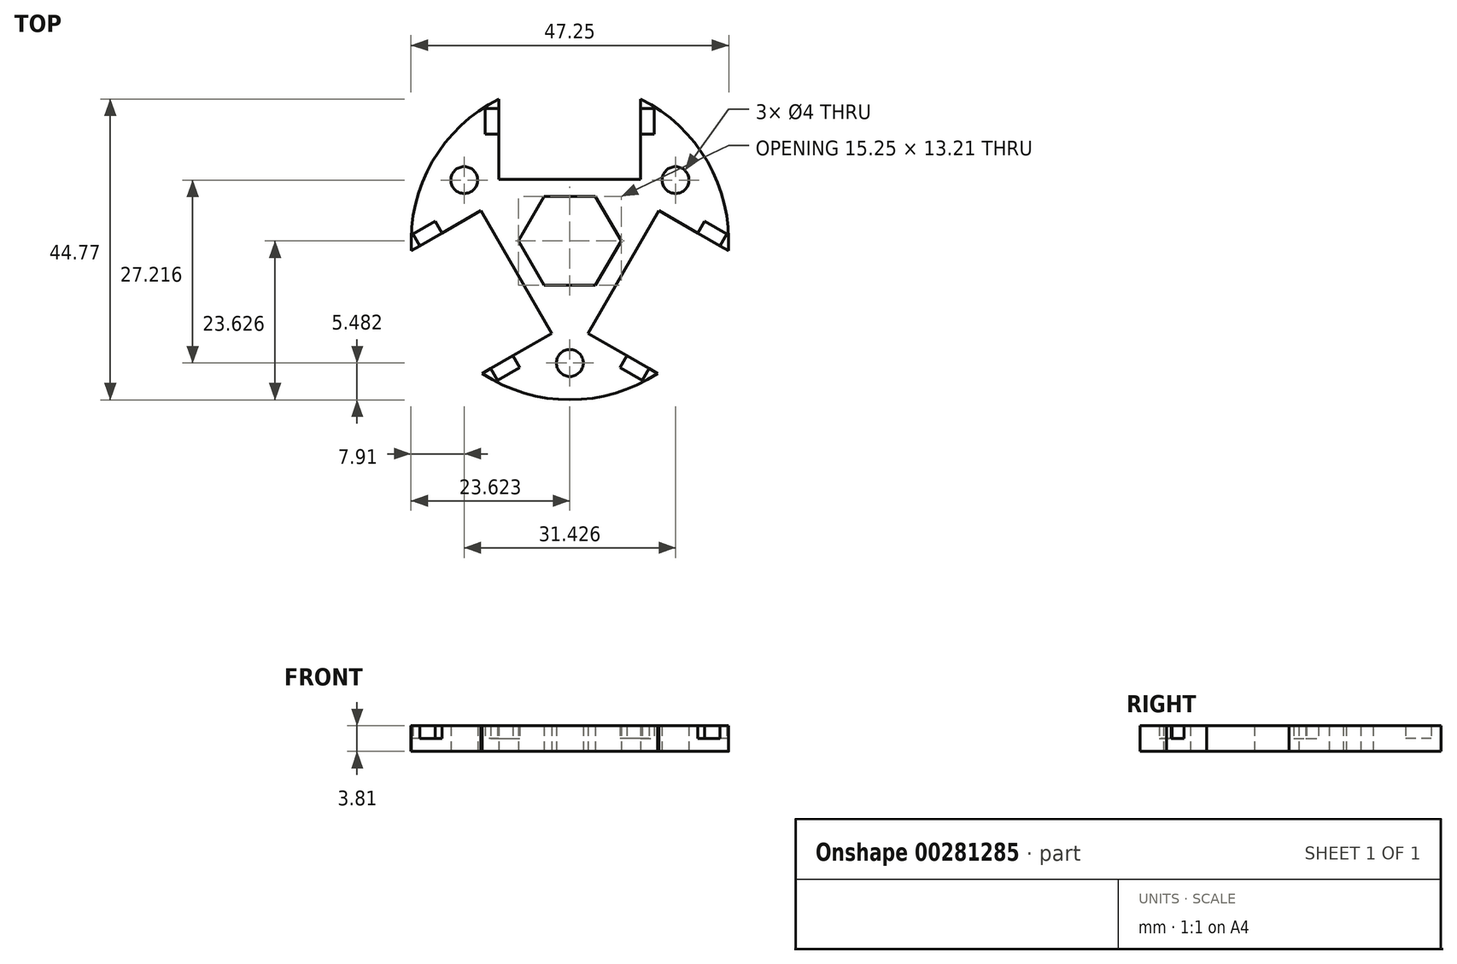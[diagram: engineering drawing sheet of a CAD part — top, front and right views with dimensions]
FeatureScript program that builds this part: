
annotation { "Feature Type Name" : "Feature", "Feature Type Description" : "" }
export const myFeature = defineFeature(function(context is Context, id is Id, definition is map)
    precondition{}
    {
        {
            var Q0;
            Q0=qCreatedBy(makeId("Top.planeOp"),FACE);
            var sketch = newSketch(context, id + "F0", { "sketchPlane" : qUnion([Q0])});
            skCircle(sketch, "E0.cCircle", {"center": v(-0.3, 28.84) * mm, "radius": 6.6 * mm, "construction": true});
            skLineSegment(sketch, "E0.0", {"start": v(-4.12, 35.44) * mm, "end": v(3.5, 35.44) * mm});
            skLineSegment(sketch, "E0.1", {"start": v(3.5, 35.44) * mm, "end": v(7.32, 28.84) * mm});
            skLineSegment(sketch, "E0.2", {"start": v(7.32, 28.84) * mm, "end": v(3.5, 22.23) * mm});
            skLineSegment(sketch, "E0.3", {"start": v(3.5, 22.23) * mm, "end": v(-4.12, 22.23) * mm});
            skLineSegment(sketch, "E0.4", {"start": v(-4.12, 22.23) * mm, "end": v(-7.93, 28.84) * mm});
            skLineSegment(sketch, "E0.5", {"start": v(-7.93, 28.84) * mm, "end": v(-4.12, 35.44) * mm});
            skPoint(sketch, "E0.0.midPoint", {"position": v(-0.3, 35.44) * mm});
            skCircle(sketch, "E1", {"center": v(-0.3, 28.84) * mm, "radius": 23.62 * mm});
            skLineSegment(sketch, "E2.bottom", {"start": v(-10.85, 49.98) * mm, "end": v(10.23, 49.98) * mm});
            skLineSegment(sketch, "E2.top", {"start": v(-10.85, 38.04) * mm, "end": v(10.23, 38.04) * mm});
            skPoint(sketch, "E3.endSnap0", {"position": v(-0.3, 49.98) * mm});
            skLineSegment(sketch, "E4.bottom", {"start": v(-10.85, 48.55) * mm, "end": v(-12.88, 48.55) * mm});
            skLineSegment(sketch, "E4.top", {"start": v(-10.85, 44.74) * mm, "end": v(-12.88, 44.74) * mm});
            skLineSegment(sketch, "E4.right", {"start": v(-12.88, 48.55) * mm, "end": v(-12.88, 44.74) * mm});
            skLineSegment(sketch, "E5", {"start": v(10.23, 49.98) * mm, "end": v(10.23, 48.55) * mm});
            skLineSegment(sketch, "E6", {"start": v(10.23, 44.74) * mm, "end": v(10.23, 38.04) * mm});
            skLineSegment(sketch, "E7", {"start": v(-10.85, 48.55) * mm, "end": v(-10.85, 49.98) * mm});
            skLineSegment(sketch, "E8", {"start": v(-10.85, 44.74) * mm, "end": v(-10.85, 38.04) * mm});
            skLineSegment(sketch, "E9.bottom", {"start": v(10.23, 48.55) * mm, "end": v(12.27, 48.55) * mm});
            skLineSegment(sketch, "E9.top", {"start": v(10.23, 44.74) * mm, "end": v(12.27, 44.74) * mm});
            skLineSegment(sketch, "E9.right", {"start": v(12.27, 48.55) * mm, "end": v(12.27, 44.74) * mm});
            skLineSegment(sketch, "E10", {"start": v(-10.85, 44.74) * mm, "end": v(-10.85, 48.55) * mm});
            skLineSegment(sketch, "E11", {"start": v(10.23, 48.55) * mm, "end": v(10.23, 44.74) * mm});
            skPoint(sketch, "E12", {"position": v(15.4, 37.9) * mm});
            skLineSegment(sketch, "E13.1.0", {"start": v(-22.65, 28.1) * mm, "end": v(-23.67, 29.87) * mm});
            skLineSegment(sketch, "E13.1.1", {"start": v(-23.67, 29.87) * mm, "end": v(-20.37, 31.77) * mm});
            skLineSegment(sketch, "E13.1.2", {"start": v(-22.65, 28.1) * mm, "end": v(-19.35, 30.01) * mm});
            skLineSegment(sketch, "E13.1.3", {"start": v(-19.35, 30.01) * mm, "end": v(-20.37, 31.77) * mm});
            skLineSegment(sketch, "E13.1.4", {"start": v(-19.35, 30.01) * mm, "end": v(-13.55, 33.36) * mm});
            skLineSegment(sketch, "E13.1.5", {"start": v(-3, 15.1) * mm, "end": v(-13.55, 33.36) * mm});
            skLineSegment(sketch, "E13.1.6", {"start": v(-8.81, 11.75) * mm, "end": v(-3, 15.1) * mm});
            skLineSegment(sketch, "E13.1.7", {"start": v(-8.81, 11.75) * mm, "end": v(-7.8, 10) * mm});
            skLineSegment(sketch, "E13.1.8", {"start": v(-8.81, 11.75) * mm, "end": v(-12.11, 9.85) * mm});
            skLineSegment(sketch, "E13.1.9", {"start": v(-12.11, 9.85) * mm, "end": v(-11.1, 8.09) * mm});
            skLineSegment(sketch, "E13.1.10", {"start": v(-11.1, 8.09) * mm, "end": v(-7.8, 10) * mm});
            skLineSegment(sketch, "E13.1.11", {"start": v(-12.11, 9.85) * mm, "end": v(-13.34, 9.14) * mm});
            skLineSegment(sketch, "E13.1.12", {"start": v(-13.34, 9.14) * mm, "end": v(-23.88, 27.4) * mm});
            skLineSegment(sketch, "E13.1.13", {"start": v(-23.88, 27.4) * mm, "end": v(-22.65, 28.1) * mm});
            skPoint(sketch, "E13.1.14", {"position": v(-16.02, 37.9) * mm});
            skLineSegment(sketch, "E13.2.0", {"start": v(11.5, 9.85) * mm, "end": v(10.48, 8.09) * mm});
            skLineSegment(sketch, "E13.2.1", {"start": v(10.48, 8.09) * mm, "end": v(7.18, 10) * mm});
            skLineSegment(sketch, "E13.2.2", {"start": v(11.5, 9.85) * mm, "end": v(8.2, 11.75) * mm});
            skLineSegment(sketch, "E13.2.3", {"start": v(8.2, 11.75) * mm, "end": v(7.18, 10) * mm});
            skLineSegment(sketch, "E13.2.4", {"start": v(8.2, 11.75) * mm, "end": v(2.4, 15.1) * mm});
            skLineSegment(sketch, "E13.2.5", {"start": v(12.93, 33.36) * mm, "end": v(2.4, 15.1) * mm});
            skLineSegment(sketch, "E13.2.6", {"start": v(18.74, 30.01) * mm, "end": v(12.93, 33.36) * mm});
            skLineSegment(sketch, "E13.2.7", {"start": v(18.74, 30.01) * mm, "end": v(19.76, 31.77) * mm});
            skLineSegment(sketch, "E13.2.8", {"start": v(18.74, 30.01) * mm, "end": v(22.04, 28.1) * mm});
            skLineSegment(sketch, "E13.2.9", {"start": v(22.04, 28.1) * mm, "end": v(23.05, 29.87) * mm});
            skLineSegment(sketch, "E13.2.10", {"start": v(23.05, 29.87) * mm, "end": v(19.76, 31.77) * mm});
            skLineSegment(sketch, "E13.2.11", {"start": v(22.04, 28.1) * mm, "end": v(23.27, 27.4) * mm});
            skLineSegment(sketch, "E13.2.12", {"start": v(23.27, 27.4) * mm, "end": v(12.73, 9.14) * mm});
            skLineSegment(sketch, "E13.2.13", {"start": v(12.73, 9.14) * mm, "end": v(11.5, 9.85) * mm});
            skPoint(sketch, "E13.2.14", {"position": v(-0.3, 10.7) * mm});
            skSolve(sketch);
        }
        {
            var Q0;
            Q0=makeQuery(id+"F0.imprint","IMPRINT",FACE,{"disambiguationData":[TD([[makeQuery(id+"F0.imprint","IMPRINT",EDGE,{"derivedFrom":sQuery(id+"F0.wireOp",EDGE,"E0.0")}),1.0]])]});
            extrude(context, id + "F1", {"entities" : qUnion([Q0]), "depth" : 3.8 * mm});
        }
        {
            var Q0;
            Q0=makeQuery(id+"F0.imprint","IMPRINT",FACE,{"disambiguationData":[TD([[makeQuery(id+"F0.imprint","IMPRINT",EDGE,{"derivedFrom":sQuery(id+"F0.wireOp",EDGE,"E0.0")}),1.0]])]});
            var Q1;
            Q1=makeQuery(id+"F0.imprint","IMPRINT",FACE,{"disambiguationData":[TD([[makeQuery(id+"F0.imprint","IMPRINT",EDGE,{"derivedFrom":sQuery(id+"F0.wireOp",EDGE,"E4.bottom")}),1.0]])]});
            var Q2;
            Q2=makeQuery(id+"F0.imprint","IMPRINT",FACE,{"disambiguationData":[TD([[makeQuery(id+"F0.imprint","IMPRINT",EDGE,{"derivedFrom":sQuery(id+"F0.wireOp",EDGE,"E9.bottom")}),-1.0]])]});
            var Q3;
            Q3=makeQuery(id+"F0.imprint","IMPRINT",FACE,{"disambiguationData":[TD([[makeQuery(id+"F0.imprint","IMPRINT",EDGE,{"derivedFrom":sQuery(id+"F0.wireOp",EDGE,"E13.2.7")}),-1.0]])]});
            var Q4;
            Q4=makeQuery(id+"F0.imprint","IMPRINT",FACE,{"disambiguationData":[TD([[makeQuery(id+"F0.imprint","IMPRINT",EDGE,{"derivedFrom":sQuery(id+"F0.wireOp",EDGE,"E13.2.0")}),-1.0]])]});
            var Q5;
            Q5=makeQuery(id+"F0.imprint","IMPRINT",FACE,{"disambiguationData":[TD([[makeQuery(id+"F0.imprint","IMPRINT",EDGE,{"derivedFrom":sQuery(id+"F0.wireOp",EDGE,"E13.1.7")}),-1.0]])]});
            var Q6;
            Q6=makeQuery(id+"F0.imprint","IMPRINT",FACE,{"disambiguationData":[TD([[makeQuery(id+"F0.imprint","IMPRINT",EDGE,{"derivedFrom":sQuery(id+"F0.wireOp",EDGE,"E13.1.0")}),-1.0]])]});
            extrude(context, id + "F2", {"entities" : qUnion([Q0, Q1, Q2, Q3, Q4, Q5, Q6]), "operationType" : NewBodyOperationType.ADD, "depth" : 1.9 * mm});
        }
        {
            var Q0;
            Q0=sQuery(id+"F0.wireOp",VERTEX,"E13.1.14");
            var Q1;
            Q1=sQuery(id+"F0.wireOp",VERTEX,"E12");
            var Q2;
            Q2=sQuery(id+"F0.wireOp",VERTEX,"E13.2.14");
            var Q3;
            Q3=makeQuery(id+"F1.opExtrude","SWEPT_BODY",BODY,{"disambiguationData":[OSD([sQuery(id+"F0.wireOp",EDGE,"E0.0"),sQuery(id+"F0.wireOp",EDGE,"E0.1"),sQuery(id+"F0.wireOp",EDGE,"E0.2"),sQuery(id+"F0.wireOp",EDGE,"E0.3"),sQuery(id+"F0.wireOp",EDGE,"E0.4"),sQuery(id+"F0.wireOp",EDGE,"E0.5"),sQuery(id+"F0.wireOp",EDGE,"E1"),sQuery(id+"F0.wireOp",EDGE,"E2.top"),sQuery(id+"F0.wireOp",EDGE,"E4.bottom"),sQuery(id+"F0.wireOp",EDGE,"E4.top"),sQuery(id+"F0.wireOp",EDGE,"E4.right"),sQuery(id+"F0.wireOp",EDGE,"E5"),sQuery(id+"F0.wireOp",EDGE,"E6"),sQuery(id+"F0.wireOp",EDGE,"E7"),sQuery(id+"F0.wireOp",EDGE,"E8"),sQuery(id+"F0.wireOp",EDGE,"E9.bottom"),sQuery(id+"F0.wireOp",EDGE,"E9.top"),sQuery(id+"F0.wireOp",EDGE,"E9.right"),sQuery(id+"F0.wireOp",EDGE,"E13.1.0"),sQuery(id+"F0.wireOp",EDGE,"E13.1.1"),sQuery(id+"F0.wireOp",EDGE,"E13.1.3"),sQuery(id+"F0.wireOp",EDGE,"E13.1.4"),sQuery(id+"F0.wireOp",EDGE,"E13.1.5"),sQuery(id+"F0.wireOp",EDGE,"E13.1.6"),sQuery(id+"F0.wireOp",EDGE,"E13.1.7"),sQuery(id+"F0.wireOp",EDGE,"E13.1.9"),sQuery(id+"F0.wireOp",EDGE,"E13.1.10"),sQuery(id+"F0.wireOp",EDGE,"E13.1.11"),sQuery(id+"F0.wireOp",EDGE,"E13.1.13"),sQuery(id+"F0.wireOp",EDGE,"E13.2.0"),sQuery(id+"F0.wireOp",EDGE,"E13.2.1"),sQuery(id+"F0.wireOp",EDGE,"E13.2.3"),sQuery(id+"F0.wireOp",EDGE,"E13.2.4"),sQuery(id+"F0.wireOp",EDGE,"E13.2.5"),sQuery(id+"F0.wireOp",EDGE,"E13.2.6"),sQuery(id+"F0.wireOp",EDGE,"E13.2.7"),sQuery(id+"F0.wireOp",EDGE,"E13.2.9"),sQuery(id+"F0.wireOp",EDGE,"E13.2.10"),sQuery(id+"F0.wireOp",EDGE,"E13.2.11"),sQuery(id+"F0.wireOp",EDGE,"E13.2.13")])]});
            hole(context, id + "F3", {"style" : HoleStyle.SIMPLE, "endStyle" : HoleEndStyle.THROUGH, "oppositeDirection" : true, "holeDiameter" : 4 * mm, "tappedDepth" : 12.7 * mm, "tapClearance" : 3, "locations" : qUnion([Q0, Q1, Q2]), "scope" : qUnion([Q3])});
        }
    });
